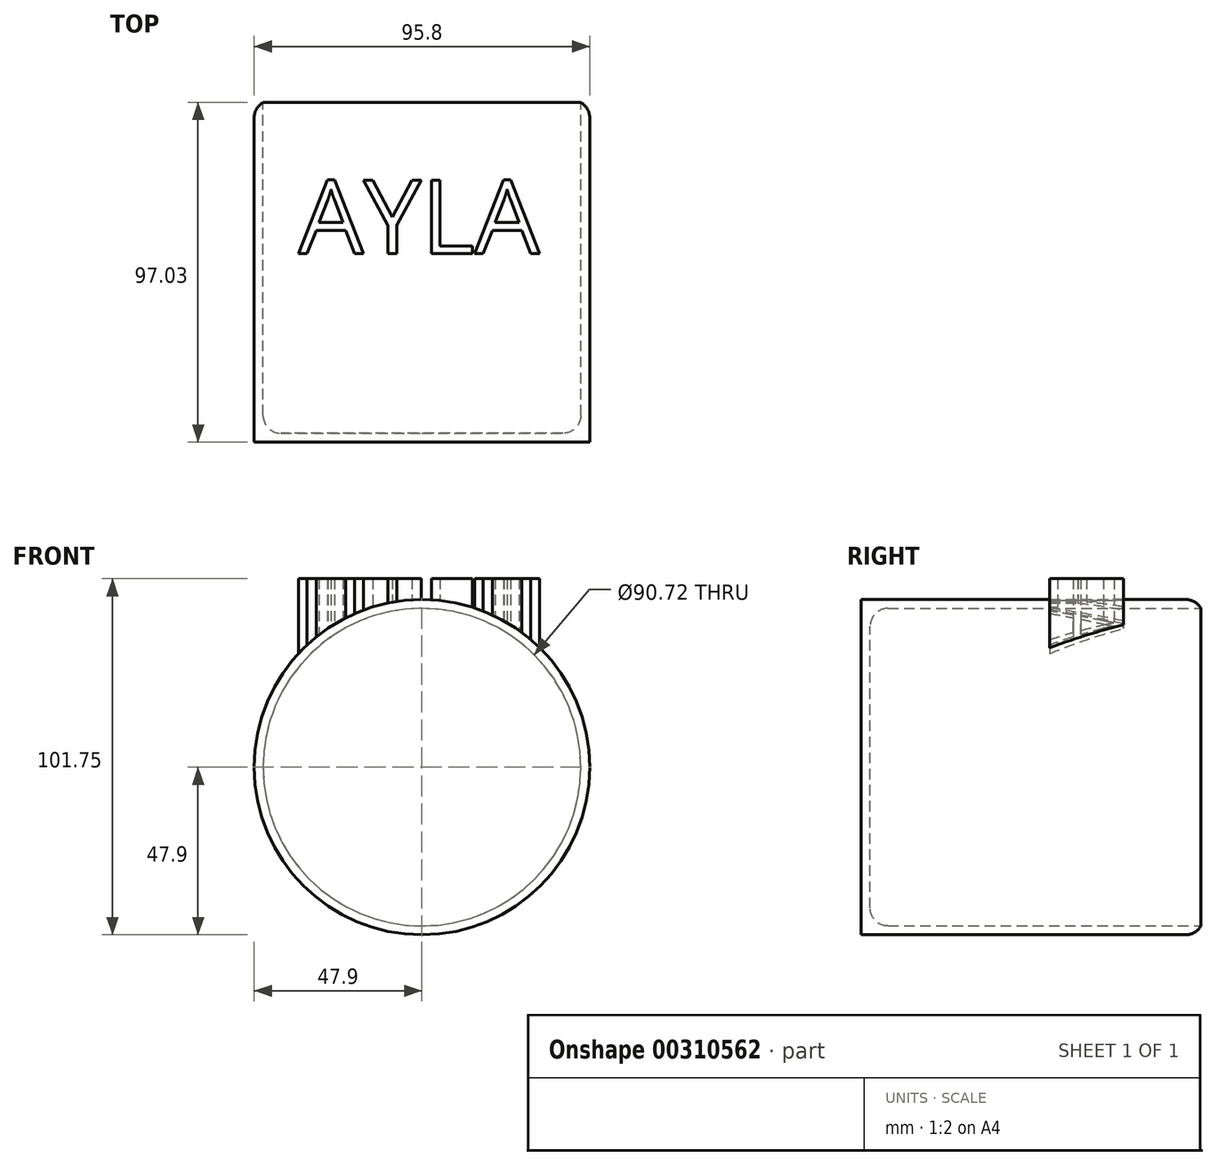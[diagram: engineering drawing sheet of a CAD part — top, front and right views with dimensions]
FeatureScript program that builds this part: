
annotation { "Feature Type Name" : "Feature", "Feature Type Description" : "" }
export const myFeature = defineFeature(function(context is Context, id is Id, definition is map)
    precondition{}
    {
        {
            var Q0;
            Q0=qCreatedBy(makeId("Front.planeOp"),FACE);
            var sketch = newSketch(context, id + "F0", { "sketchPlane" : qUnion([Q0])});
            skCircle(sketch, "E0", {"center": v(0, 0) * mm, "radius": 47.9 * mm});
            skSolve(sketch);
        }
        {
            var Q0;
            Q0=makeQuery(id+"F0.imprint","IMPRINT",FACE,{"disambiguationData":[TD([[makeQuery(id+"F0.imprint","IMPRINT",EDGE,{"derivedFrom":sQuery(id+"F0.wireOp",EDGE,"E0")}),1.0]])]});
            extrude(context, id + "F1", {"entities" : qUnion([Q0]), "depth" : 97.03 * mm});
        }
        {
            var Q0;
            Q0=qCreatedBy(makeId("Top.planeOp"),FACE);
            var sketch = newSketch(context, id + "F2", { "sketchPlane" : qUnion([Q0])});
            skText(sketch, "E1", { "text": "AYLA", "fontName": "OpenSans-Regular.ttf"});
            const initialGuessF2  = {"E1": [-0.03525, -0.0432, 1, 0, 0.02115]};
            skSetInitialGuess(sketch, initialGuessF2);
            skSolve(sketch);
        }
        {
            var Q0;
            Q0 = qSketchRegion(id + "F2", true);
            extrude(context, id + "F3", {"entities" : qUnion([Q0]), "operationType" : NewBodyOperationType.ADD, "depth" : 53.85 * mm});
        }
        {
            var Q0;
            Q0=makeQuery(id+"F1.opExtrude","CAP_FACE",FACE,{"disambiguationData":[OSD([sQuery(id+"F0.wireOp",EDGE,"E0")])],"isStart":true});
            shell(context, id + "F4", {"entities" : qUnion([Q0]), "thickness" : 2.54 * mm});
        }
        {
            var Q0;
            {var subQ0=sQuery(id+"F0.wireOp",EDGE,"E0");Q0=makeQuery(id+"F4.opShell","OFFSET_FACE",FACE,{"disambiguationData":[OSD([subQ0]),TDD([makeQuery(id+"F1.opExtrude","CAP_FACE",FACE,{"disambiguationData":[OSD([subQ0])],"isStart":false})])]});}
            fillet(context, id + "F5", {"entities" : qUnion([Q0]), "radius" : 5.08 * mm, "tangentPropagation" : true, "allowEdgeOverflow" : false});
        }
        {
            var Q0;
            Q0=makeQuery(id+"F1.opExtrude","CAP_EDGE",EDGE,{"disambiguationData":[OSD([sQuery(id+"F0.wireOp",EDGE,"E0")])],"isStart":true});
            fillet(context, id + "F6", {"entities" : qUnion([Q0]), "radius" : 5.08 * mm, "tangentPropagation" : true, "allowEdgeOverflow" : false});
        }
    });
